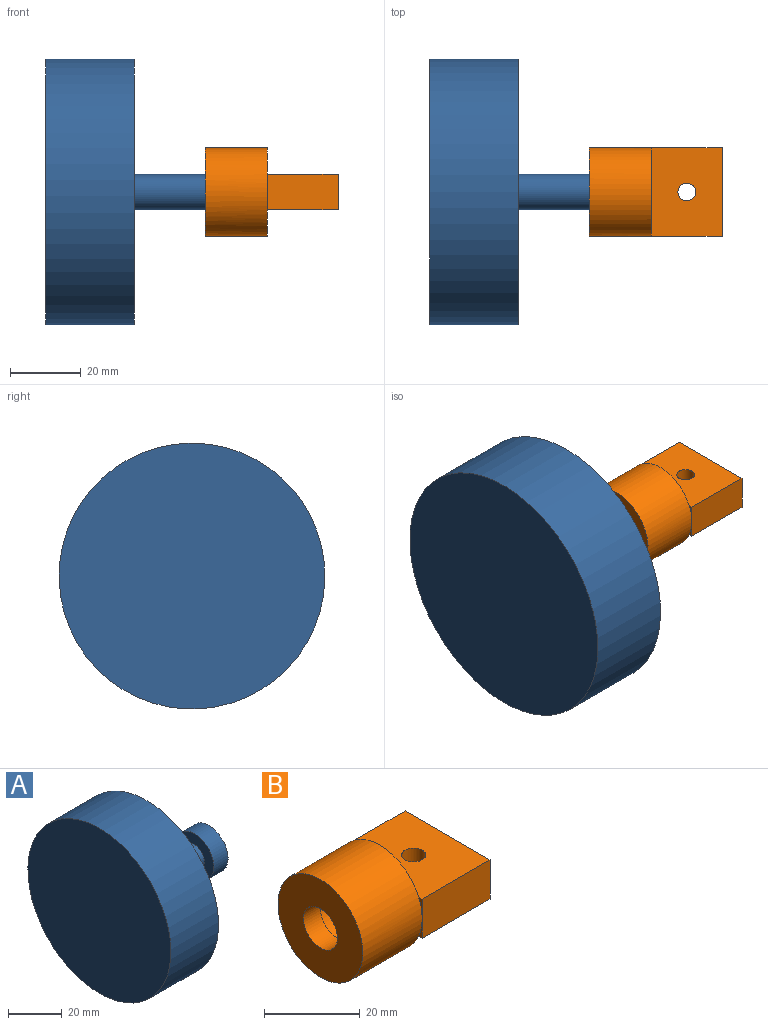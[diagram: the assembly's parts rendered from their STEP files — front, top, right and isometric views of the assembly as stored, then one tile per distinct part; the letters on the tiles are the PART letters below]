
ASSEMBLY  parts=2 mates=1
PART A: 9 faces, bbox 57.5x75x75 mm
  f0: plane 20x20mm, normal (1,0,0), area 314.2mm2, adj f1
  f1: cylinder r=10mm len=20mm, axis (1,0,0), area 471.2mm2, adj f0,f2
  f2: plane 20x20mm, normal (-1,0,0), area 235.6mm2, adj f1,f3
  f3: cylinder r=5mm len=45mm, axis (1,0,0), area 1413.7mm2, adj f2,f4
  f4: plane 65x65mm, normal (1,0,0), area 3239.8mm2, adj f3,f5
  f5: cylinder r=32.5mm len=65mm, axis (1,0,0), area 4084.1mm2, adj f4,f6
  f6: plane 75x75mm, normal (1,0,0), area 1099.6mm2, adj f5,f7
  f7: cylinder r=37.5mm len=75mm, axis (1,0,0), area 5890.5mm2, adj f6,f8
  f8: plane 75x75mm, normal (-1,0,0), area 4417.9mm2, adj f7
PART B: 18 faces, bbox 37.5x25x25 mm
  f0: plane 22.91x7.5mm, normal (1,0,0), area 123.9mm2, adj f2,f11
  f1: plane 22.91x7.5mm, normal (1,0,0), area 123.9mm2, adj f2,f16
  f2: cylinder r=12.5mm len=25mm, axis (1,0,0), area 1374.4mm2, adj f0,f1,f3,f8,f9,f14,f15
  f3: plane 25x25mm, normal (-1,0,0), area 412.3mm2, adj f2,f4
  f4: cylinder r=5mm len=10mm, axis (1,0,0), area 157.1mm2, adj f3,f5
  f5: plane 15x15mm, normal (1,0,0), area 98.2mm2, adj f4,f6
  f6: cylinder r=7.5mm len=15mm, axis (1,0,0), area 353.4mm2, adj f5,f7
  f7: plane 15x15mm, normal (-1,0,0), area 176.7mm2, adj f6
  f8: plane 5x1.04mm, normal (-1,0,0), area 1.7mm2, adj f2,f11,f13
  f9: plane 5x1.04mm, normal (-1,0,0), area 1.7mm2, adj f2,f11,f12
  f10: plane 25x10mm, normal (1,0,0), area 250mm2, adj f11,f12,f13,f16
  f11: plane 25x20mm, normal (0,0,1), area 480.4mm2, adj f0,f8,f9,f10,f12,f13,f17
  f12: plane 20x10mm, normal (0,-1,0), area 200mm2, adj f9,f10,f11,f14,f16
  f13: plane 20x10mm, normal (0,1,0), area 200mm2, adj f8,f10,f11,f15,f16
  f14: plane 5x1.04mm, normal (-1,0,0), area 1.7mm2, adj f2,f12,f16
  f15: plane 5x1.04mm, normal (-1,0,0), area 1.7mm2, adj f2,f13,f16
  f16: plane 25x20mm, normal (0,0,-1), area 480.4mm2, adj f1,f10,f12,f13,f14,f15,f17
  f17: cylinder r=2.5mm len=10mm, axis (0,0,1), area 157.1mm2, adj f11,f16
PLACE A rot(axis=(-1,0,0),60deg) t=(-9.76,34.47,4.96)mm
PLACE B t=(47.74,34.47,4.96)mm fixed
MATE revolute A.f1 <-> B.f2  axis (-1,0,0) through (40.24,34.47,4.96)mm
